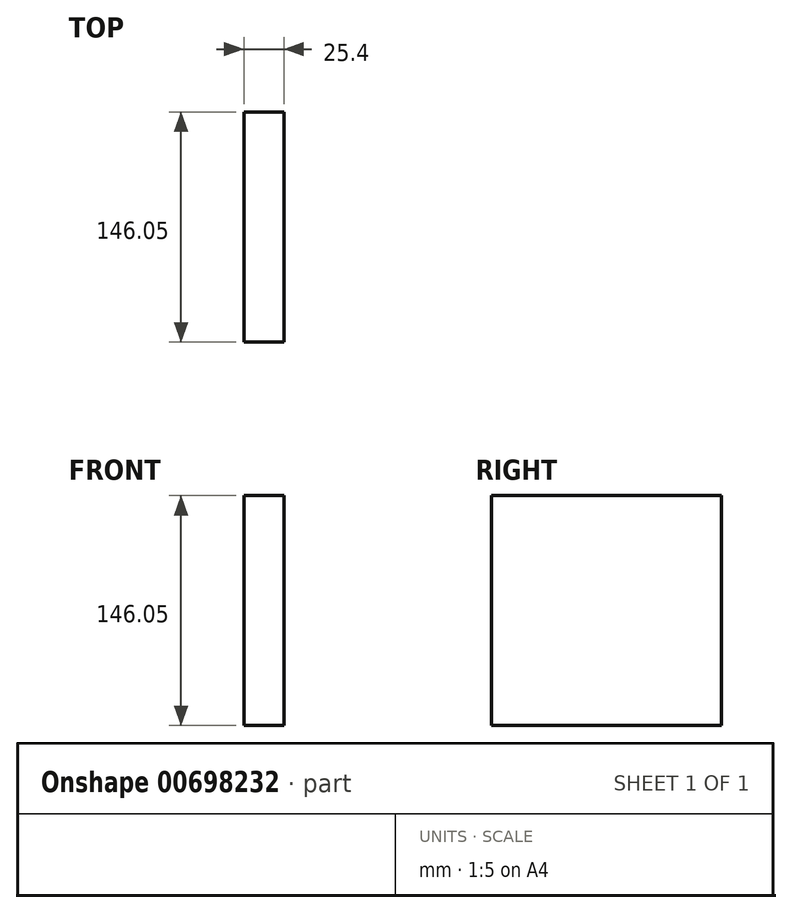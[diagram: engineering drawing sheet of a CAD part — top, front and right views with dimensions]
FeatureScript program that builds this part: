
annotation { "Feature Type Name" : "Feature", "Feature Type Description" : "" }
export const myFeature = defineFeature(function(context is Context, id is Id, definition is map)
    precondition{}
    {
        {
            var Q0;
            Q0=qCreatedBy(makeId("Right.planeOp"),FACE);
            var sketch = newSketch(context, id + "F0", { "sketchPlane" : qUnion([Q0])});
            skLineSegment(sketch, "E0.bottom", {"start": v(-103.88, 54.35) * mm, "end": v(42.17, 54.35) * mm});
            skLineSegment(sketch, "E0.top", {"start": v(-103.88, -91.7) * mm, "end": v(42.17, -91.7) * mm});
            skLineSegment(sketch, "E0.left", {"start": v(-103.88, 54.35) * mm, "end": v(-103.88, -91.7) * mm});
            skLineSegment(sketch, "E0.right", {"start": v(42.17, 54.35) * mm, "end": v(42.17, -91.7) * mm});
            skSolve(sketch);
        }
        {
            var Q0;
            Q0=makeQuery(id+"F0.imprint","IMPRINT",FACE,{"disambiguationData":[TD([[makeQuery(id+"F0.imprint","IMPRINT",EDGE,{"derivedFrom":sQuery(id+"F0.wireOp",EDGE,"E0.bottom")}),-1.0]])]});
            var sketch = newSketch(context, id + "F1", { "sketchPlane" : qUnion([Q0])});
            skSolve(sketch);
        }
        {
            var Q0;
            Q0=makeQuery(id+"F1.imprint","IMPRINT",FACE,{"disambiguationData":[TD([[makeQuery(id+"F1.imprint","IMPRINT",EDGE,{"derivedFrom":makeQuery(id+"F0.imprint","IMPRINT",EDGE,{"derivedFrom":sQuery(id+"F0.wireOp",EDGE,"E0.bottom")})}),-1.0]])]});
            var sketch = newSketch(context, id + "F2", { "sketchPlane" : qUnion([Q0])});
            skSolve(sketch);
        }
        {
            var Q0;
            Q0=makeQuery(id+"F2.imprint","IMPRINT",FACE,{"disambiguationData":[TD([[makeQuery(id+"F2.imprint","IMPRINT",EDGE,{"derivedFrom":makeQuery(id+"F1.imprint","IMPRINT",EDGE,{"derivedFrom":makeQuery(id+"F0.imprint","IMPRINT",EDGE,{"derivedFrom":sQuery(id+"F0.wireOp",EDGE,"E0.bottom")})})}),-1.0]])]});
            extrude(context, id + "F3", {"entities" : qUnion([Q0]), "depth" : 25.4 * mm, "offsetDistance" : 25.4 * mm});
        }
    });
